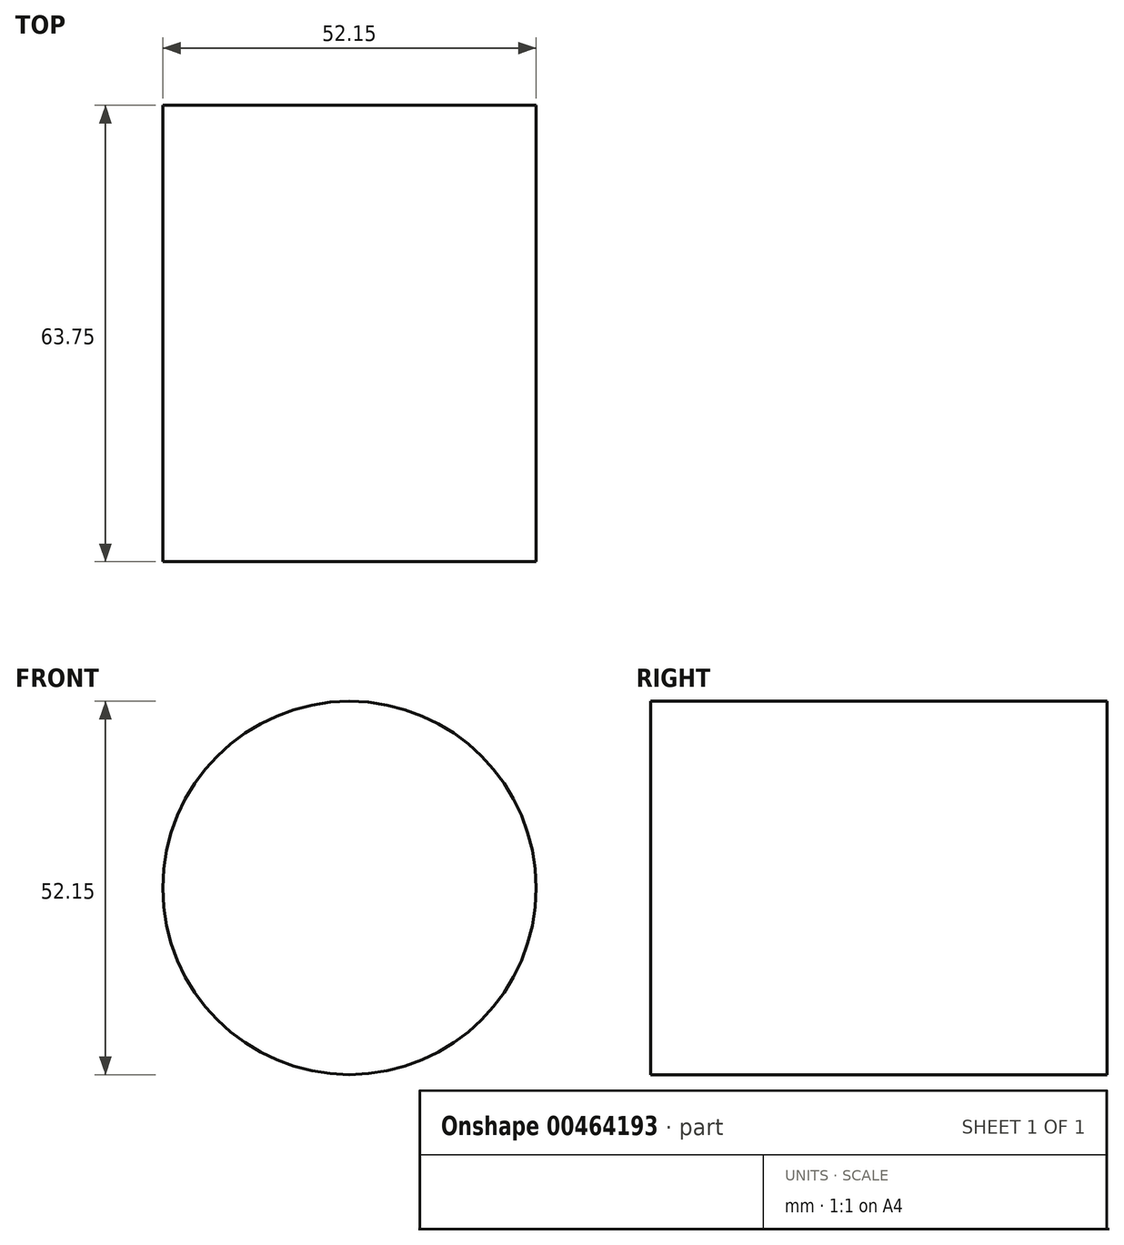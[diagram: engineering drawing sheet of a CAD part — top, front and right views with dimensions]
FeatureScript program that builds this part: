
annotation { "Feature Type Name" : "Feature", "Feature Type Description" : "" }
export const myFeature = defineFeature(function(context is Context, id is Id, definition is map)
    precondition{}
    {
        {
            var Q0;
            Q0=qCreatedBy(makeId("Front.planeOp"),FACE);
            var sketch = newSketch(context, id + "F0", { "sketchPlane" : qUnion([Q0])});
            skCircle(sketch, "E0", {"center": v(-99.7, 44.87) * mm, "radius": 26.07 * mm});
            skSolve(sketch);
        }
        {
            var Q0;
            Q0=sQuery(id+"F0.wireOp",EDGE,"E0");
            extrude(context, id + "F1", {"bodyType" : ToolBodyType.SURFACE, "surfaceEntities" : qUnion([Q0]), "depth" : 63.75 * mm});
        }
    });
